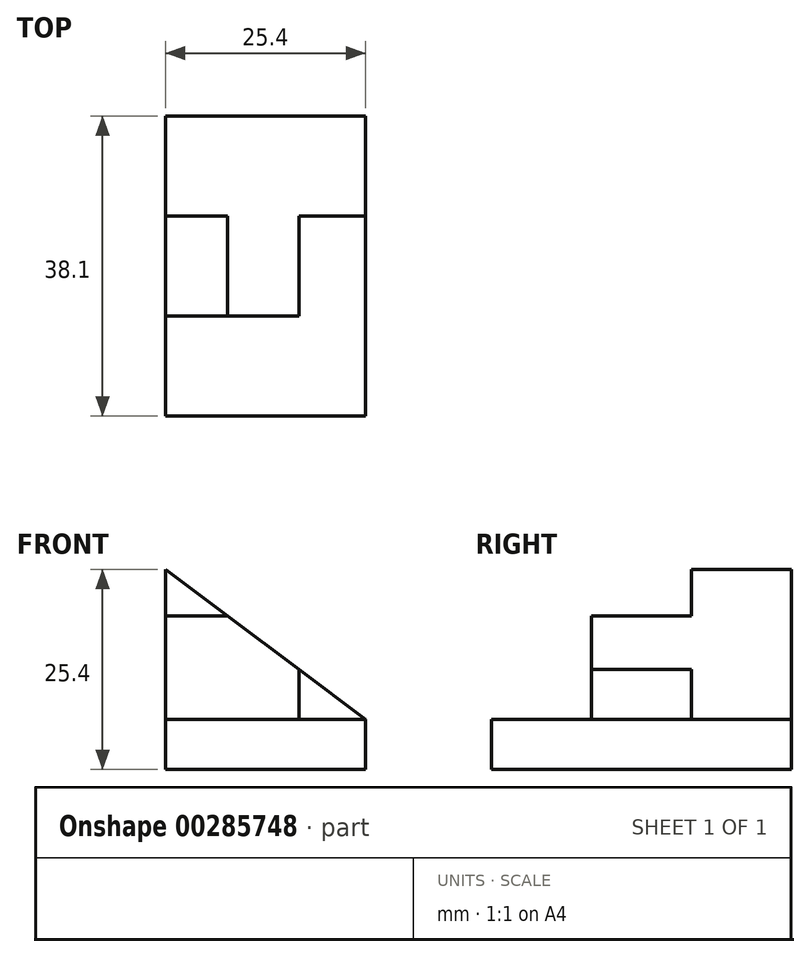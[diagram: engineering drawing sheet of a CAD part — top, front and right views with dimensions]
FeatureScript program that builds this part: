
annotation { "Feature Type Name" : "Feature", "Feature Type Description" : "" }
export const myFeature = defineFeature(function(context is Context, id is Id, definition is map)
    precondition{}
    {
        {
            var Q0;
            Q0=qCreatedBy(makeId("Front.planeOp"),FACE);
            var sketch = newSketch(context, id + "F0", { "sketchPlane" : qUnion([Q0])});
            skLineSegment(sketch, "E0.bottom", {"start": v(0, 0) * mm, "end": v(25.4, 0) * mm});
            skLineSegment(sketch, "E0.top", {"start": v(0, 6.35) * mm, "end": v(25.4, 6.35) * mm});
            skLineSegment(sketch, "E0.left", {"start": v(0, 0) * mm, "end": v(0, 6.35) * mm});
            skLineSegment(sketch, "E0.right", {"start": v(25.4, 0) * mm, "end": v(25.4, 6.35) * mm});
            skSolve(sketch);
        }
        {
            var Q0;
            Q0 = qSketchRegion(id + "F0", true);
            extrude(context, id + "F1", {"entities" : qUnion([Q0]), "depth" : 38.1 * mm});
        }
        {
            var Q0;
            Q0=makeQuery(id+"F1.opExtrude","CAP_FACE",FACE,{"disambiguationData":[OSD([sQuery(id+"F0.wireOp",EDGE,"E0.bottom"),sQuery(id+"F0.wireOp",EDGE,"E0.top"),sQuery(id+"F0.wireOp",EDGE,"E0.left"),sQuery(id+"F0.wireOp",EDGE,"E0.right")])],"isStart":true});
            var sketch = newSketch(context, id + "F2", { "sketchPlane" : qUnion([Q0])});
            skLineSegment(sketch, "E1", {"start": v(0, 6.35) * mm, "end": v(0, 25.4) * mm});
            skLineSegment(sketch, "E2", {"start": v(0, 25.4) * mm, "end": v(-25.4, 6.35) * mm});
            skLineSegment(sketch, "E3", {"start": v(-25.4, 6.35) * mm, "end": v(0, 6.35) * mm});
            skSolve(sketch);
        }
        {
            var Q0;
            Q0 = qSketchRegion(id + "F2", true);
            extrude(context, id + "F3", {"entities" : qUnion([Q0]), "operationType" : NewBodyOperationType.ADD, "oppositeDirection" : true, "depth" : 12.7 * mm});
        }
        {
            var Q0;
            Q0=makeQuery(id+"F3.opExtrude","CAP_FACE",FACE,{"disambiguationData":[OSD([sQuery(id+"F2.wireOp",EDGE,"E1"),sQuery(id+"F2.wireOp",EDGE,"E2"),sQuery(id+"F2.wireOp",EDGE,"E3")])],"isStart":false});
            var sketch = newSketch(context, id + "F4", { "sketchPlane" : qUnion([Q0])});
            skLineSegment(sketch, "E4", {"start": v(0, 6.35) * mm, "end": v(0, 19.5) * mm});
            skLineSegment(sketch, "E5", {"start": v(0, 19.5) * mm, "end": v(7.88, 19.5) * mm});
            skLineSegment(sketch, "E6", {"start": v(7.88, 19.5) * mm, "end": v(16.95, 12.68) * mm});
            skLineSegment(sketch, "E7", {"start": v(16.95, 12.68) * mm, "end": v(16.95, 6.35) * mm});
            skLineSegment(sketch, "E8", {"start": v(16.95, 6.35) * mm, "end": v(0, 6.35) * mm});
            skSolve(sketch);
        }
        {
            var Q0;
            Q0 = qSketchRegion(id + "F4", true);
            extrude(context, id + "F5", {"entities" : qUnion([Q0]), "operationType" : NewBodyOperationType.ADD, "depth" : 12.7 * mm});
        }
    });
